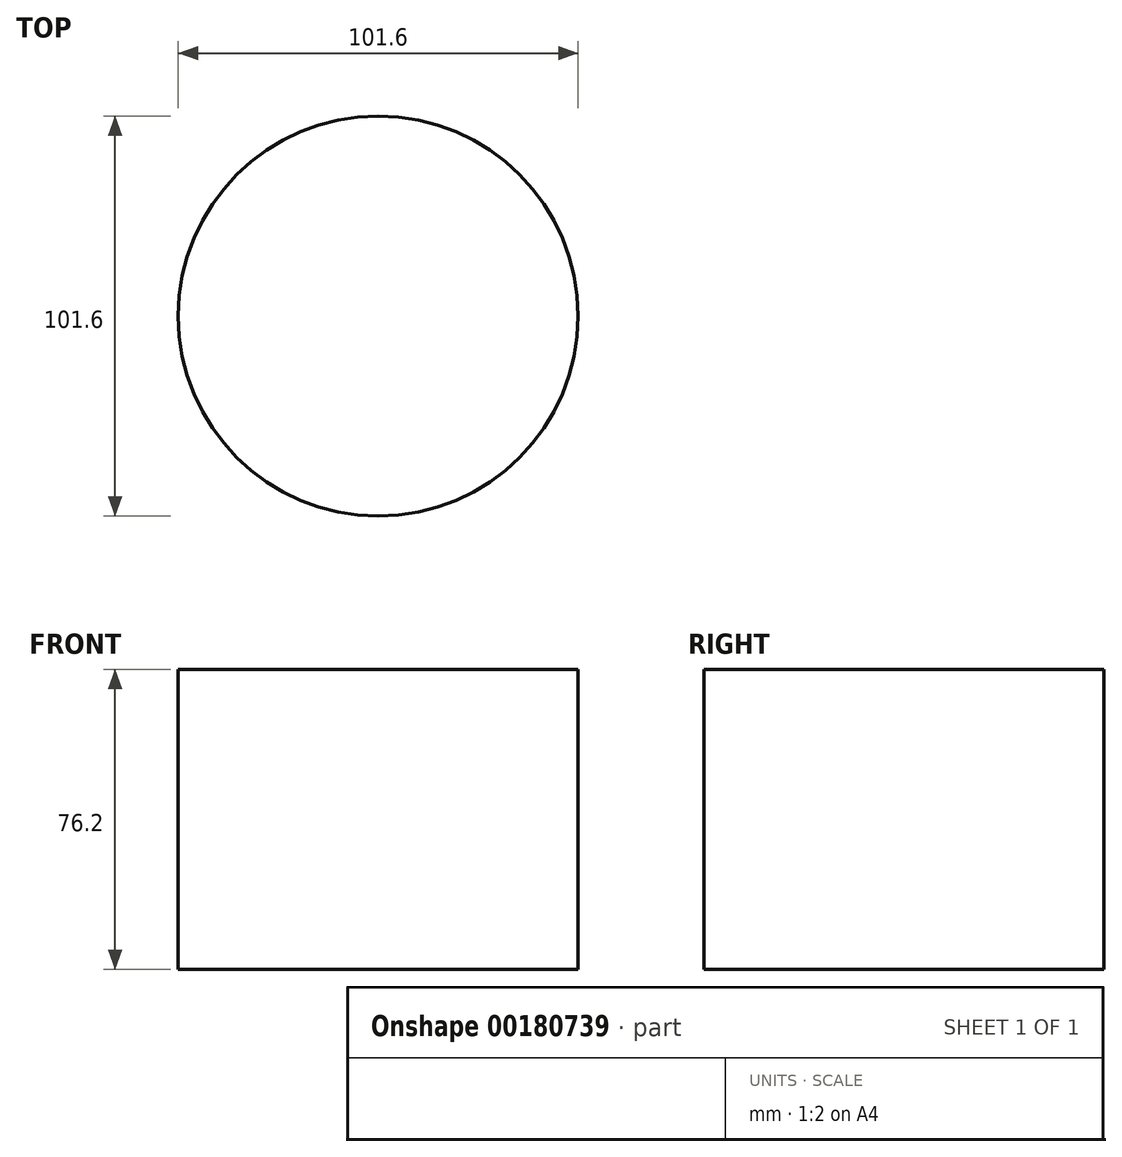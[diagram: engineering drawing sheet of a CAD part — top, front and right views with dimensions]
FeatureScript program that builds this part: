
annotation { "Feature Type Name" : "Feature", "Feature Type Description" : "" }
export const myFeature = defineFeature(function(context is Context, id is Id, definition is map)
    precondition{}
    {
        {
            var Q0;
            Q0=qCreatedBy(makeId("Top.planeOp"),FACE);
            var sketch = newSketch(context, id + "F0", { "sketchPlane" : qUnion([Q0])});
            skCircle(sketch, "E0", {"center": v(0, 0) * mm, "radius": 50.8 * mm});
            skSolve(sketch);
        }
        {
            var Q0;
            Q0=makeQuery(id+"F0.imprint","IMPRINT",FACE,{"disambiguationData":[TD([[makeQuery(id+"F0.imprint","IMPRINT",EDGE,{"derivedFrom":sQuery(id+"F0.wireOp",EDGE,"E0")}),1.0]])]});
            extrude(context, id + "F1", {"entities" : qUnion([Q0]), "depth" : 76.2 * mm});
        }
    });
